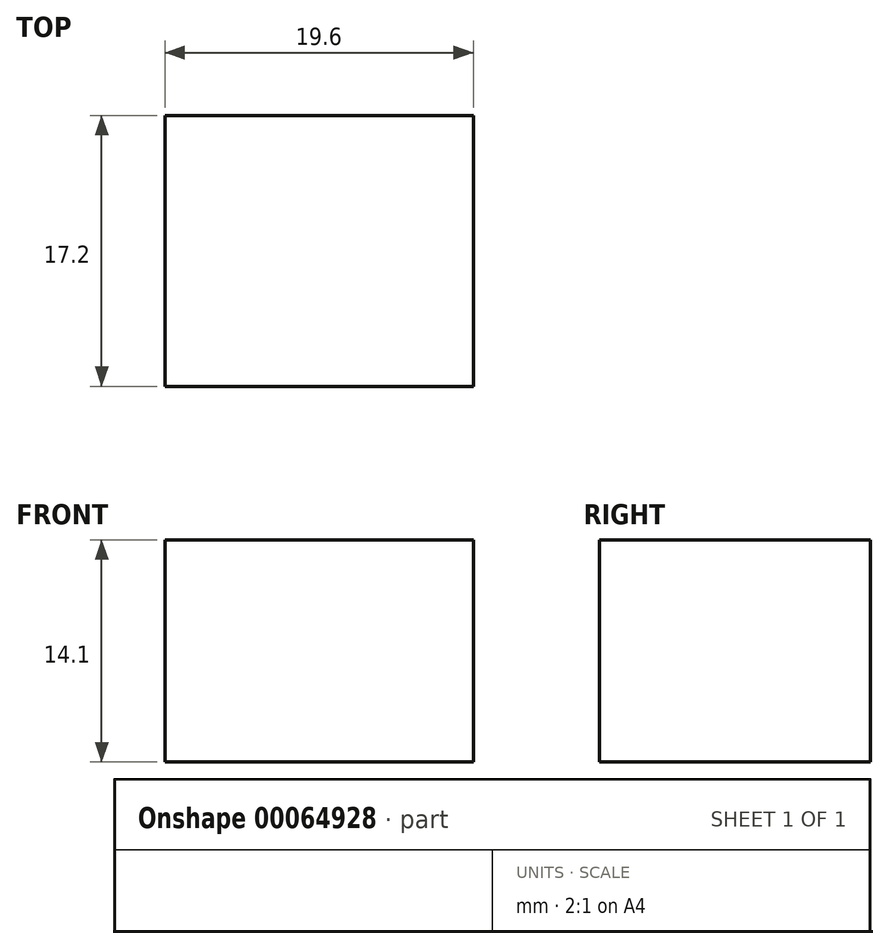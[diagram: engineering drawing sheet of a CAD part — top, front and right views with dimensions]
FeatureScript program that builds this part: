
annotation { "Feature Type Name" : "Feature", "Feature Type Description" : "" }
export const myFeature = defineFeature(function(context is Context, id is Id, definition is map)
    precondition{}
    {
        {
            var Q0;
            Q0=qCreatedBy(makeId("Top.planeOp"),FACE);
            var sketch = newSketch(context, id + "F0", { "sketchPlane" : qUnion([Q0])});
            skLineSegment(sketch, "E0.bottom", {"start": v(0, 0) * mm, "end": v(19.6, 0) * mm});
            skLineSegment(sketch, "E0.top", {"start": v(0, 17.2) * mm, "end": v(19.6, 17.2) * mm});
            skLineSegment(sketch, "E0.left", {"start": v(0, 0) * mm, "end": v(0, 17.2) * mm});
            skLineSegment(sketch, "E0.right", {"start": v(19.6, 0) * mm, "end": v(19.6, 17.2) * mm});
            skSolve(sketch);
        }
        {
            var Q0;
            Q0=makeQuery(id+"F0.imprint","IMPRINT",FACE,{"disambiguationData":[TD([[makeQuery(id+"F0.imprint","IMPRINT",EDGE,{"derivedFrom":sQuery(id+"F0.wireOp",EDGE,"E0.bottom")}),1.0]])]});
            extrude(context, id + "F1", {"entities" : qUnion([Q0]), "depth" : 14.1 * mm});
        }
    });
